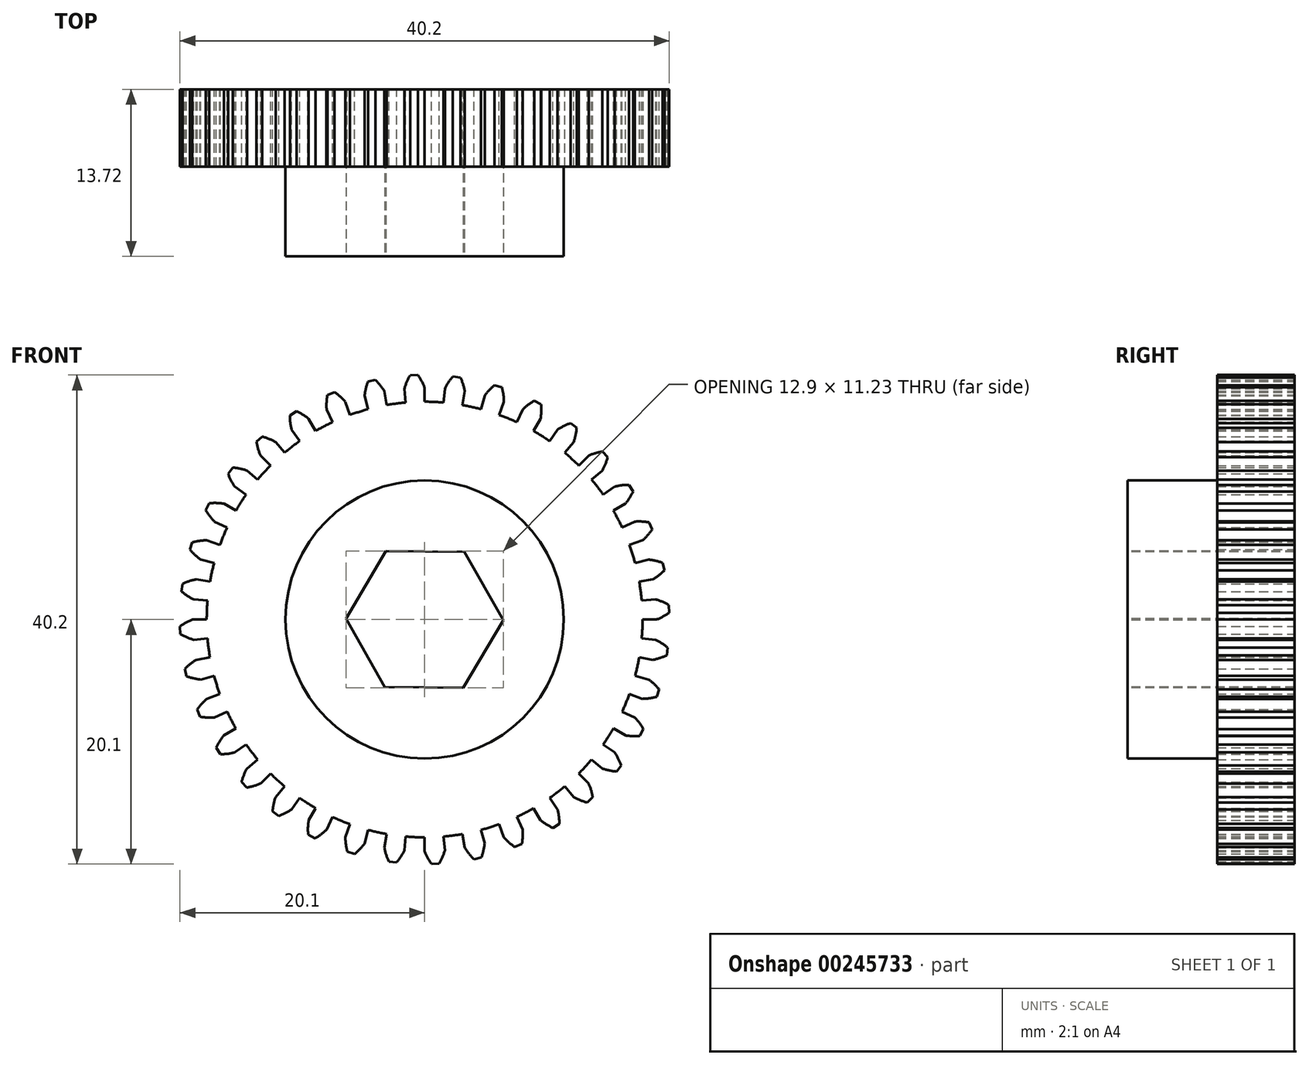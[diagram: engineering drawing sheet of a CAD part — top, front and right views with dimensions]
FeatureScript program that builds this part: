
annotation { "Feature Type Name" : "Feature", "Feature Type Description" : "" }
export const myFeature = defineFeature(function(context is Context, id is Id, definition is map)
    precondition{}
    {
        {
            var Q0;
            Q0=qCreatedBy(makeId("Front.planeOp"),FACE);
            var sketch = newSketch(context, id + "F0", { "sketchPlane" : qUnion([Q0])});
            skArc(sketch, "E0", {"start": v(-4.45, 17.34) * mm, "mid": v(-5.38, 17.07) * mm, "end": v(-6.3, 16.75) * mm});
            skLineSegment(sketch, "E1.trimOffspring", {"start": v(0, 23.81) * mm, "end": v(0, 30.83) * mm});
            skArc(sketch, "E2.trimOffspring", {"start": v(0, 19.05) * mm, "mid": v(-0.25, 19.6) * mm, "end": v(-0.56, 20.1) * mm});
            skArc(sketch, "E3.MirrorCS", {"start": v(-1.66, 18.98) * mm, "mid": v(-1.46, 19.54) * mm, "end": v(-1.2, 20.07) * mm});
            skLineSegment(sketch, "E4.trimOffspring", {"start": v(-1.56, 17.83) * mm, "end": v(-1.66, 18.98) * mm});
            skLineSegment(sketch, "E5.trimOffspring", {"start": v(0, 17.9) * mm, "end": v(0, 19.05) * mm});
            skArc(sketch, "E6.trimOffspring", {"start": v(0, 17.9) * mm, "mid": v(-0.1, 17.9) * mm, "end": v(-0.2, 17.9) * mm});
            skArc(sketch, "E7", {"start": v(-1.56, 17.84) * mm, "mid": v(-2.34, 17.75) * mm, "end": v(-3.1, 17.63) * mm});
            skLineSegment(sketch, "E8", {"start": v(-1.2, 20.07) * mm, "end": v(-0.56, 20.1) * mm});
            skLineSegment(sketch, "E9.1.0", {"start": v(-4.63, 17.3) * mm, "end": v(-4.93, 18.4) * mm});
            skArc(sketch, "E9.1.1", {"start": v(-4.93, 18.4) * mm, "mid": v(-4.83, 18.99) * mm, "end": v(-4.66, 19.56) * mm});
            skLineSegment(sketch, "E9.1.2", {"start": v(-4.66, 19.56) * mm, "end": v(-4.04, 19.7) * mm});
            skArc(sketch, "E9.1.3", {"start": v(-3.3, 18.76) * mm, "mid": v(-3.65, 19.25) * mm, "end": v(-4.04, 19.7) * mm});
            skLineSegment(sketch, "E9.1.4", {"start": v(-3.1, 17.63) * mm, "end": v(-3.3, 18.76) * mm});
            skLineSegment(sketch, "E9.2.0", {"start": v(-7.57, 16.22) * mm, "end": v(-8.05, 17.27) * mm});
            skArc(sketch, "E9.2.1", {"start": v(-8.05, 17.27) * mm, "mid": v(-8.05, 17.86) * mm, "end": v(-7.98, 18.45) * mm});
            skLineSegment(sketch, "E9.2.2", {"start": v(-7.98, 18.45) * mm, "end": v(-7.4, 18.7) * mm});
            skArc(sketch, "E9.2.3", {"start": v(-6.52, 17.9) * mm, "mid": v(-6.93, 18.32) * mm, "end": v(-7.4, 18.7) * mm});
            skLineSegment(sketch, "E9.2.4", {"start": v(-6.12, 16.82) * mm, "end": v(-6.52, 17.9) * mm});
            skLineSegment(sketch, "E9.3.0", {"start": v(-10.27, 14.66) * mm, "end": v(-10.93, 15.6) * mm});
            skArc(sketch, "E9.3.1", {"start": v(-10.93, 15.6) * mm, "mid": v(-11.03, 16.19) * mm, "end": v(-11.07, 16.78) * mm});
            skLineSegment(sketch, "E9.3.2", {"start": v(-11.07, 16.78) * mm, "end": v(-10.53, 17.12) * mm});
            skArc(sketch, "E9.3.3", {"start": v(-9.52, 16.5) * mm, "mid": v(-10, 16.84) * mm, "end": v(-10.53, 17.12) * mm});
            skLineSegment(sketch, "E9.3.4", {"start": v(-8.95, 15.5) * mm, "end": v(-9.53, 16.5) * mm});
            skLineSegment(sketch, "E9.4.0", {"start": v(-12.66, 12.66) * mm, "end": v(-13.47, 13.47) * mm});
            skArc(sketch, "E9.4.1", {"start": v(-13.47, 13.47) * mm, "mid": v(-13.68, 14.03) * mm, "end": v(-13.81, 14.6) * mm});
            skLineSegment(sketch, "E9.4.2", {"start": v(-13.81, 14.6) * mm, "end": v(-13.35, 15.03) * mm});
            skArc(sketch, "E9.4.3", {"start": v(-12.25, 14.6) * mm, "mid": v(-12.78, 14.85) * mm, "end": v(-13.35, 15.03) * mm});
            skLineSegment(sketch, "E9.4.4", {"start": v(-11.5, 13.71) * mm, "end": v(-12.25, 14.6) * mm});
            skLineSegment(sketch, "E9.5.0", {"start": v(-14.66, 10.27) * mm, "end": v(-15.6, 10.93) * mm});
            skArc(sketch, "E9.5.1", {"start": v(-15.6, 10.93) * mm, "mid": v(-15.9, 11.44) * mm, "end": v(-16.14, 11.99) * mm});
            skLineSegment(sketch, "E9.5.2", {"start": v(-16.14, 11.99) * mm, "end": v(-15.76, 12.49) * mm});
            skArc(sketch, "E9.5.3", {"start": v(-14.6, 12.25) * mm, "mid": v(-15.17, 12.4) * mm, "end": v(-15.76, 12.49) * mm});
            skLineSegment(sketch, "E9.5.4", {"start": v(-13.71, 11.5) * mm, "end": v(-14.6, 12.25) * mm});
            skLineSegment(sketch, "E9.6.0", {"start": v(-16.22, 7.57) * mm, "end": v(-17.27, 8.05) * mm});
            skArc(sketch, "E9.6.1", {"start": v(-17.27, 8.05) * mm, "mid": v(-17.65, 8.5) * mm, "end": v(-17.98, 9) * mm});
            skLineSegment(sketch, "E9.6.2", {"start": v(-17.98, 9) * mm, "end": v(-17.68, 9.56) * mm});
            skArc(sketch, "E9.6.3", {"start": v(-16.5, 9.53) * mm, "mid": v(-17.09, 9.58) * mm, "end": v(-17.68, 9.56) * mm});
            skLineSegment(sketch, "E9.6.4", {"start": v(-15.5, 8.95) * mm, "end": v(-16.5, 9.53) * mm});
            skLineSegment(sketch, "E9.7.0", {"start": v(-17.3, 4.63) * mm, "end": v(-18.4, 4.93) * mm});
            skArc(sketch, "E9.7.1", {"start": v(-18.4, 4.93) * mm, "mid": v(-18.86, 5.3) * mm, "end": v(-19.27, 5.74) * mm});
            skLineSegment(sketch, "E9.7.2", {"start": v(-19.27, 5.74) * mm, "end": v(-19.08, 6.35) * mm});
            skArc(sketch, "E9.7.3", {"start": v(-17.9, 6.52) * mm, "mid": v(-18.5, 6.47) * mm, "end": v(-19.08, 6.35) * mm});
            skLineSegment(sketch, "E9.7.4", {"start": v(-16.82, 6.12) * mm, "end": v(-17.9, 6.52) * mm});
            skLineSegment(sketch, "E9.8.0", {"start": v(-17.83, 1.56) * mm, "end": v(-18.98, 1.66) * mm});
            skArc(sketch, "E9.8.1", {"start": v(-18.98, 1.66) * mm, "mid": v(-19.5, 1.95) * mm, "end": v(-19.97, 2.31) * mm});
            skLineSegment(sketch, "E9.8.2", {"start": v(-19.97, 2.31) * mm, "end": v(-19.89, 2.94) * mm});
            skArc(sketch, "E9.8.3", {"start": v(-18.76, 3.3) * mm, "mid": v(-19.34, 3.16) * mm, "end": v(-19.89, 2.94) * mm});
            skLineSegment(sketch, "E9.8.4", {"start": v(-17.63, 3.1) * mm, "end": v(-18.76, 3.3) * mm});
            skLineSegment(sketch, "E9.9.0", {"start": v(-17.83, -1.56) * mm, "end": v(-18.98, -1.66) * mm});
            skArc(sketch, "E9.9.1", {"start": v(-18.98, -1.66) * mm, "mid": v(-19.54, -1.46) * mm, "end": v(-20.07, -1.2) * mm});
            skLineSegment(sketch, "E9.9.2", {"start": v(-20.07, -1.2) * mm, "end": v(-20.1, -0.56) * mm});
            skArc(sketch, "E9.9.3", {"start": v(-19.05, 0) * mm, "mid": v(-19.6, -0.25) * mm, "end": v(-20.1, -0.56) * mm});
            skLineSegment(sketch, "E9.9.4", {"start": v(-17.9, 0) * mm, "end": v(-19.05, 0) * mm});
            skLineSegment(sketch, "E9.10.0", {"start": v(-17.3, -4.63) * mm, "end": v(-18.4, -4.93) * mm});
            skArc(sketch, "E9.10.1", {"start": v(-18.4, -4.93) * mm, "mid": v(-18.99, -4.83) * mm, "end": v(-19.56, -4.66) * mm});
            skLineSegment(sketch, "E9.10.2", {"start": v(-19.56, -4.66) * mm, "end": v(-19.7, -4.04) * mm});
            skArc(sketch, "E9.10.3", {"start": v(-18.76, -3.3) * mm, "mid": v(-19.25, -3.65) * mm, "end": v(-19.7, -4.04) * mm});
            skLineSegment(sketch, "E9.10.4", {"start": v(-17.63, -3.1) * mm, "end": v(-18.76, -3.3) * mm});
            skLineSegment(sketch, "E9.11.0", {"start": v(-16.22, -7.57) * mm, "end": v(-17.27, -8.05) * mm});
            skArc(sketch, "E9.11.1", {"start": v(-17.27, -8.05) * mm, "mid": v(-17.86, -8.05) * mm, "end": v(-18.45, -7.98) * mm});
            skLineSegment(sketch, "E9.11.2", {"start": v(-18.45, -7.98) * mm, "end": v(-18.7, -7.4) * mm});
            skArc(sketch, "E9.11.3", {"start": v(-17.9, -6.52) * mm, "mid": v(-18.32, -6.93) * mm, "end": v(-18.7, -7.4) * mm});
            skLineSegment(sketch, "E9.11.4", {"start": v(-16.82, -6.12) * mm, "end": v(-17.9, -6.52) * mm});
            skLineSegment(sketch, "E9.12.0", {"start": v(-14.66, -10.27) * mm, "end": v(-15.6, -10.93) * mm});
            skArc(sketch, "E9.12.1", {"start": v(-15.6, -10.93) * mm, "mid": v(-16.19, -11.03) * mm, "end": v(-16.78, -11.07) * mm});
            skLineSegment(sketch, "E9.12.2", {"start": v(-16.78, -11.07) * mm, "end": v(-17.12, -10.53) * mm});
            skArc(sketch, "E9.12.3", {"start": v(-16.5, -9.52) * mm, "mid": v(-16.84, -10) * mm, "end": v(-17.12, -10.53) * mm});
            skLineSegment(sketch, "E9.12.4", {"start": v(-15.5, -8.95) * mm, "end": v(-16.5, -9.52) * mm});
            skLineSegment(sketch, "E9.13.0", {"start": v(-12.66, -12.66) * mm, "end": v(-13.47, -13.47) * mm});
            skArc(sketch, "E9.13.1", {"start": v(-13.47, -13.47) * mm, "mid": v(-14.03, -13.68) * mm, "end": v(-14.6, -13.81) * mm});
            skLineSegment(sketch, "E9.13.2", {"start": v(-14.6, -13.81) * mm, "end": v(-15.03, -13.35) * mm});
            skArc(sketch, "E9.13.3", {"start": v(-14.6, -12.25) * mm, "mid": v(-14.85, -12.78) * mm, "end": v(-15.03, -13.35) * mm});
            skLineSegment(sketch, "E9.13.4", {"start": v(-13.71, -11.5) * mm, "end": v(-14.6, -12.25) * mm});
            skLineSegment(sketch, "E9.14.0", {"start": v(-10.27, -14.66) * mm, "end": v(-10.93, -15.6) * mm});
            skArc(sketch, "E9.14.1", {"start": v(-10.93, -15.6) * mm, "mid": v(-11.44, -15.9) * mm, "end": v(-11.99, -16.14) * mm});
            skLineSegment(sketch, "E9.14.2", {"start": v(-11.99, -16.14) * mm, "end": v(-12.49, -15.76) * mm});
            skArc(sketch, "E9.14.3", {"start": v(-12.25, -14.6) * mm, "mid": v(-12.4, -15.17) * mm, "end": v(-12.49, -15.76) * mm});
            skLineSegment(sketch, "E9.14.4", {"start": v(-11.5, -13.71) * mm, "end": v(-12.25, -14.6) * mm});
            skLineSegment(sketch, "E9.15.0", {"start": v(-7.57, -16.22) * mm, "end": v(-8.05, -17.27) * mm});
            skArc(sketch, "E9.15.1", {"start": v(-8.05, -17.27) * mm, "mid": v(-8.5, -17.65) * mm, "end": v(-9, -17.98) * mm});
            skLineSegment(sketch, "E9.15.2", {"start": v(-9, -17.98) * mm, "end": v(-9.56, -17.68) * mm});
            skArc(sketch, "E9.15.3", {"start": v(-9.53, -16.5) * mm, "mid": v(-9.58, -17.09) * mm, "end": v(-9.56, -17.68) * mm});
            skLineSegment(sketch, "E9.15.4", {"start": v(-8.95, -15.5) * mm, "end": v(-9.53, -16.5) * mm});
            skLineSegment(sketch, "E9.16.0", {"start": v(-4.63, -17.3) * mm, "end": v(-4.93, -18.4) * mm});
            skArc(sketch, "E9.16.1", {"start": v(-4.93, -18.4) * mm, "mid": v(-5.3, -18.86) * mm, "end": v(-5.74, -19.27) * mm});
            skLineSegment(sketch, "E9.16.2", {"start": v(-5.74, -19.27) * mm, "end": v(-6.35, -19.08) * mm});
            skArc(sketch, "E9.16.3", {"start": v(-6.52, -17.9) * mm, "mid": v(-6.47, -18.5) * mm, "end": v(-6.35, -19.08) * mm});
            skLineSegment(sketch, "E9.16.4", {"start": v(-6.12, -16.82) * mm, "end": v(-6.52, -17.9) * mm});
            skLineSegment(sketch, "E9.17.0", {"start": v(-1.56, -17.83) * mm, "end": v(-1.66, -18.98) * mm});
            skArc(sketch, "E9.17.1", {"start": v(-1.66, -18.98) * mm, "mid": v(-1.95, -19.5) * mm, "end": v(-2.31, -19.97) * mm});
            skLineSegment(sketch, "E9.17.2", {"start": v(-2.31, -19.97) * mm, "end": v(-2.94, -19.89) * mm});
            skArc(sketch, "E9.17.3", {"start": v(-3.3, -18.76) * mm, "mid": v(-3.16, -19.34) * mm, "end": v(-2.94, -19.89) * mm});
            skLineSegment(sketch, "E9.17.4", {"start": v(-3.1, -17.63) * mm, "end": v(-3.3, -18.76) * mm});
            skLineSegment(sketch, "E9.18.0", {"start": v(1.56, -17.83) * mm, "end": v(1.66, -18.98) * mm});
            skArc(sketch, "E9.18.1", {"start": v(1.66, -18.98) * mm, "mid": v(1.46, -19.54) * mm, "end": v(1.2, -20.07) * mm});
            skLineSegment(sketch, "E9.18.2", {"start": v(1.2, -20.07) * mm, "end": v(0.56, -20.1) * mm});
            skArc(sketch, "E9.18.3", {"start": v(0, -19.05) * mm, "mid": v(0.25, -19.6) * mm, "end": v(0.56, -20.1) * mm});
            skLineSegment(sketch, "E9.18.4", {"start": v(0, -17.9) * mm, "end": v(0, -19.05) * mm});
            skLineSegment(sketch, "E9.19.0", {"start": v(4.63, -17.3) * mm, "end": v(4.93, -18.4) * mm});
            skArc(sketch, "E9.19.1", {"start": v(4.93, -18.4) * mm, "mid": v(4.83, -18.99) * mm, "end": v(4.66, -19.56) * mm});
            skLineSegment(sketch, "E9.19.2", {"start": v(4.66, -19.56) * mm, "end": v(4.04, -19.7) * mm});
            skArc(sketch, "E9.19.3", {"start": v(3.3, -18.76) * mm, "mid": v(3.65, -19.25) * mm, "end": v(4.04, -19.7) * mm});
            skLineSegment(sketch, "E9.19.4", {"start": v(3.1, -17.63) * mm, "end": v(3.3, -18.76) * mm});
            skLineSegment(sketch, "E9.20.0", {"start": v(7.57, -16.22) * mm, "end": v(8.05, -17.27) * mm});
            skArc(sketch, "E9.20.1", {"start": v(8.05, -17.27) * mm, "mid": v(8.05, -17.86) * mm, "end": v(7.98, -18.45) * mm});
            skLineSegment(sketch, "E9.20.2", {"start": v(7.98, -18.45) * mm, "end": v(7.4, -18.7) * mm});
            skArc(sketch, "E9.20.3", {"start": v(6.52, -17.9) * mm, "mid": v(6.93, -18.32) * mm, "end": v(7.4, -18.7) * mm});
            skLineSegment(sketch, "E9.20.4", {"start": v(6.12, -16.82) * mm, "end": v(6.52, -17.9) * mm});
            skLineSegment(sketch, "E9.21.0", {"start": v(10.27, -14.66) * mm, "end": v(10.93, -15.6) * mm});
            skArc(sketch, "E9.21.1", {"start": v(10.93, -15.6) * mm, "mid": v(11.03, -16.19) * mm, "end": v(11.07, -16.78) * mm});
            skLineSegment(sketch, "E9.21.2", {"start": v(11.07, -16.78) * mm, "end": v(10.53, -17.12) * mm});
            skArc(sketch, "E9.21.3", {"start": v(9.52, -16.5) * mm, "mid": v(10, -16.84) * mm, "end": v(10.53, -17.12) * mm});
            skLineSegment(sketch, "E9.21.4", {"start": v(8.95, -15.5) * mm, "end": v(9.53, -16.5) * mm});
            skLineSegment(sketch, "E9.22.0", {"start": v(12.66, -12.66) * mm, "end": v(13.47, -13.47) * mm});
            skArc(sketch, "E9.22.1", {"start": v(13.47, -13.47) * mm, "mid": v(13.68, -14.03) * mm, "end": v(13.81, -14.6) * mm});
            skLineSegment(sketch, "E9.22.2", {"start": v(13.81, -14.6) * mm, "end": v(13.35, -15.03) * mm});
            skArc(sketch, "E9.22.3", {"start": v(12.25, -14.6) * mm, "mid": v(12.78, -14.85) * mm, "end": v(13.35, -15.03) * mm});
            skLineSegment(sketch, "E9.22.4", {"start": v(11.5, -13.71) * mm, "end": v(12.25, -14.6) * mm});
            skLineSegment(sketch, "E9.23.0", {"start": v(14.66, -10.27) * mm, "end": v(15.6, -10.93) * mm});
            skArc(sketch, "E9.23.1", {"start": v(15.6, -10.93) * mm, "mid": v(15.9, -11.44) * mm, "end": v(16.14, -11.99) * mm});
            skLineSegment(sketch, "E9.23.2", {"start": v(16.14, -11.99) * mm, "end": v(15.76, -12.49) * mm});
            skArc(sketch, "E9.23.3", {"start": v(14.6, -12.25) * mm, "mid": v(15.17, -12.4) * mm, "end": v(15.76, -12.49) * mm});
            skLineSegment(sketch, "E9.23.4", {"start": v(13.71, -11.5) * mm, "end": v(14.6, -12.25) * mm});
            skLineSegment(sketch, "E9.24.0", {"start": v(16.22, -7.57) * mm, "end": v(17.27, -8.05) * mm});
            skArc(sketch, "E9.24.1", {"start": v(17.27, -8.05) * mm, "mid": v(17.65, -8.5) * mm, "end": v(17.98, -9) * mm});
            skLineSegment(sketch, "E9.24.2", {"start": v(17.98, -9) * mm, "end": v(17.68, -9.56) * mm});
            skArc(sketch, "E9.24.3", {"start": v(16.5, -9.53) * mm, "mid": v(17.09, -9.58) * mm, "end": v(17.68, -9.56) * mm});
            skLineSegment(sketch, "E9.24.4", {"start": v(15.5, -8.95) * mm, "end": v(16.5, -9.53) * mm});
            skLineSegment(sketch, "E9.25.0", {"start": v(17.3, -4.63) * mm, "end": v(18.4, -4.93) * mm});
            skArc(sketch, "E9.25.1", {"start": v(18.4, -4.93) * mm, "mid": v(18.86, -5.3) * mm, "end": v(19.27, -5.74) * mm});
            skLineSegment(sketch, "E9.25.2", {"start": v(19.27, -5.74) * mm, "end": v(19.08, -6.35) * mm});
            skArc(sketch, "E9.25.3", {"start": v(17.9, -6.52) * mm, "mid": v(18.5, -6.47) * mm, "end": v(19.08, -6.35) * mm});
            skLineSegment(sketch, "E9.25.4", {"start": v(16.82, -6.12) * mm, "end": v(17.9, -6.52) * mm});
            skLineSegment(sketch, "E9.26.0", {"start": v(17.83, -1.56) * mm, "end": v(18.98, -1.66) * mm});
            skArc(sketch, "E9.26.1", {"start": v(18.98, -1.66) * mm, "mid": v(19.5, -1.95) * mm, "end": v(19.97, -2.31) * mm});
            skLineSegment(sketch, "E9.26.2", {"start": v(19.97, -2.31) * mm, "end": v(19.89, -2.94) * mm});
            skArc(sketch, "E9.26.3", {"start": v(18.76, -3.3) * mm, "mid": v(19.34, -3.16) * mm, "end": v(19.89, -2.94) * mm});
            skLineSegment(sketch, "E9.26.4", {"start": v(17.63, -3.1) * mm, "end": v(18.76, -3.3) * mm});
            skLineSegment(sketch, "E9.27.0", {"start": v(17.83, 1.56) * mm, "end": v(18.98, 1.66) * mm});
            skArc(sketch, "E9.27.1", {"start": v(18.98, 1.66) * mm, "mid": v(19.54, 1.46) * mm, "end": v(20.07, 1.2) * mm});
            skLineSegment(sketch, "E9.27.2", {"start": v(20.07, 1.2) * mm, "end": v(20.1, 0.56) * mm});
            skArc(sketch, "E9.27.3", {"start": v(19.05, 0) * mm, "mid": v(19.6, 0.25) * mm, "end": v(20.1, 0.56) * mm});
            skLineSegment(sketch, "E9.27.4", {"start": v(17.9, 0) * mm, "end": v(19.05, 0) * mm});
            skLineSegment(sketch, "E9.28.0", {"start": v(17.3, 4.63) * mm, "end": v(18.4, 4.93) * mm});
            skArc(sketch, "E9.28.1", {"start": v(18.4, 4.93) * mm, "mid": v(18.99, 4.83) * mm, "end": v(19.56, 4.66) * mm});
            skLineSegment(sketch, "E9.28.2", {"start": v(19.56, 4.66) * mm, "end": v(19.7, 4.04) * mm});
            skArc(sketch, "E9.28.3", {"start": v(18.76, 3.3) * mm, "mid": v(19.25, 3.65) * mm, "end": v(19.7, 4.04) * mm});
            skLineSegment(sketch, "E9.28.4", {"start": v(17.63, 3.1) * mm, "end": v(18.76, 3.3) * mm});
            skLineSegment(sketch, "E9.29.0", {"start": v(16.22, 7.57) * mm, "end": v(17.27, 8.05) * mm});
            skArc(sketch, "E9.29.1", {"start": v(17.27, 8.05) * mm, "mid": v(17.86, 8.05) * mm, "end": v(18.45, 7.98) * mm});
            skLineSegment(sketch, "E9.29.2", {"start": v(18.45, 7.98) * mm, "end": v(18.7, 7.4) * mm});
            skArc(sketch, "E9.29.3", {"start": v(17.9, 6.52) * mm, "mid": v(18.32, 6.93) * mm, "end": v(18.7, 7.4) * mm});
            skLineSegment(sketch, "E9.29.4", {"start": v(16.82, 6.12) * mm, "end": v(17.9, 6.52) * mm});
            skLineSegment(sketch, "E9.30.0", {"start": v(14.66, 10.27) * mm, "end": v(15.6, 10.93) * mm});
            skArc(sketch, "E9.30.1", {"start": v(15.6, 10.93) * mm, "mid": v(16.19, 11.03) * mm, "end": v(16.78, 11.07) * mm});
            skLineSegment(sketch, "E9.30.2", {"start": v(16.78, 11.07) * mm, "end": v(17.12, 10.53) * mm});
            skArc(sketch, "E9.30.3", {"start": v(16.5, 9.52) * mm, "mid": v(16.84, 10) * mm, "end": v(17.12, 10.53) * mm});
            skLineSegment(sketch, "E9.30.4", {"start": v(15.5, 8.95) * mm, "end": v(16.5, 9.52) * mm});
            skLineSegment(sketch, "E9.31.0", {"start": v(12.66, 12.66) * mm, "end": v(13.47, 13.47) * mm});
            skArc(sketch, "E9.31.1", {"start": v(13.47, 13.47) * mm, "mid": v(14.03, 13.68) * mm, "end": v(14.6, 13.81) * mm});
            skLineSegment(sketch, "E9.31.2", {"start": v(14.6, 13.81) * mm, "end": v(15.03, 13.35) * mm});
            skArc(sketch, "E9.31.3", {"start": v(14.6, 12.25) * mm, "mid": v(14.85, 12.78) * mm, "end": v(15.03, 13.35) * mm});
            skLineSegment(sketch, "E9.31.4", {"start": v(13.71, 11.5) * mm, "end": v(14.6, 12.25) * mm});
            skLineSegment(sketch, "E9.32.0", {"start": v(10.27, 14.66) * mm, "end": v(10.93, 15.6) * mm});
            skArc(sketch, "E9.32.1", {"start": v(10.93, 15.6) * mm, "mid": v(11.44, 15.9) * mm, "end": v(11.99, 16.14) * mm});
            skLineSegment(sketch, "E9.32.2", {"start": v(11.99, 16.14) * mm, "end": v(12.49, 15.76) * mm});
            skArc(sketch, "E9.32.3", {"start": v(12.25, 14.6) * mm, "mid": v(12.4, 15.17) * mm, "end": v(12.49, 15.76) * mm});
            skLineSegment(sketch, "E9.32.4", {"start": v(11.5, 13.71) * mm, "end": v(12.25, 14.6) * mm});
            skLineSegment(sketch, "E9.33.0", {"start": v(7.57, 16.22) * mm, "end": v(8.05, 17.27) * mm});
            skArc(sketch, "E9.33.1", {"start": v(8.05, 17.27) * mm, "mid": v(8.5, 17.65) * mm, "end": v(9, 17.98) * mm});
            skLineSegment(sketch, "E9.33.2", {"start": v(9, 17.98) * mm, "end": v(9.56, 17.68) * mm});
            skArc(sketch, "E9.33.3", {"start": v(9.53, 16.5) * mm, "mid": v(9.58, 17.09) * mm, "end": v(9.56, 17.68) * mm});
            skLineSegment(sketch, "E9.33.4", {"start": v(8.95, 15.5) * mm, "end": v(9.52, 16.5) * mm});
            skLineSegment(sketch, "E9.34.0", {"start": v(4.63, 17.3) * mm, "end": v(4.93, 18.4) * mm});
            skArc(sketch, "E9.34.1", {"start": v(4.93, 18.4) * mm, "mid": v(5.3, 18.86) * mm, "end": v(5.74, 19.27) * mm});
            skLineSegment(sketch, "E9.34.2", {"start": v(5.74, 19.27) * mm, "end": v(6.35, 19.08) * mm});
            skArc(sketch, "E9.34.3", {"start": v(6.52, 17.9) * mm, "mid": v(6.47, 18.5) * mm, "end": v(6.35, 19.08) * mm});
            skLineSegment(sketch, "E9.34.4", {"start": v(6.12, 16.82) * mm, "end": v(6.52, 17.9) * mm});
            skLineSegment(sketch, "E9.35.0", {"start": v(1.56, 17.83) * mm, "end": v(1.66, 18.98) * mm});
            skArc(sketch, "E9.35.1", {"start": v(1.66, 18.98) * mm, "mid": v(1.95, 19.5) * mm, "end": v(2.31, 19.97) * mm});
            skLineSegment(sketch, "E9.35.2", {"start": v(2.31, 19.97) * mm, "end": v(2.94, 19.89) * mm});
            skArc(sketch, "E9.35.3", {"start": v(3.3, 18.76) * mm, "mid": v(3.16, 19.34) * mm, "end": v(2.94, 19.89) * mm});
            skLineSegment(sketch, "E9.35.4", {"start": v(3.1, 17.63) * mm, "end": v(3.3, 18.76) * mm});
            skArc(sketch, "E10.trimOffspring", {"start": v(-1.37, 17.85) * mm, "mid": v(-1.46, 17.84) * mm, "end": v(-1.56, 17.83) * mm});
            skArc(sketch, "E11.trimOffspring", {"start": v(1.56, 17.84) * mm, "mid": v(0.78, 17.89) * mm, "end": v(0, 17.9) * mm});
            skArc(sketch, "E12.trimOffspring", {"start": v(4.63, 17.3) * mm, "mid": v(3.88, 17.48) * mm, "end": v(3.1, 17.63) * mm});
            skArc(sketch, "E13.trimOffspring", {"start": v(4.82, 17.24) * mm, "mid": v(3.87, 17.48) * mm, "end": v(2.92, 17.66) * mm});
            skArc(sketch, "E14.trimOffspring", {"start": v(7.57, 16.23) * mm, "mid": v(6.85, 16.54) * mm, "end": v(6.12, 16.82) * mm});
            skArc(sketch, "E15.trimOffspring", {"start": v(7.74, 16.14) * mm, "mid": v(6.85, 16.54) * mm, "end": v(5.94, 16.89) * mm});
            skArc(sketch, "E16.trimOffspring", {"start": v(10.27, 14.67) * mm, "mid": v(9.62, 15.1) * mm, "end": v(8.95, 15.5) * mm});
            skArc(sketch, "E17.trimOffspring", {"start": v(10.43, 14.55) * mm, "mid": v(9.62, 15.1) * mm, "end": v(8.78, 15.6) * mm});
            skArc(sketch, "E18.trimOffspring", {"start": v(12.8, 12.52) * mm, "mid": v(12.1, 13.2) * mm, "end": v(11.36, 13.84) * mm});
            skArc(sketch, "E19.trimOffspring", {"start": v(14.67, 10.27) * mm, "mid": v(14.2, 10.9) * mm, "end": v(13.72, 11.5) * mm});
            skArc(sketch, "E20.trimOffspring", {"start": v(14.77, 10.1) * mm, "mid": v(14.2, 10.9) * mm, "end": v(13.59, 11.65) * mm});
            skArc(sketch, "E21.trimOffspring", {"start": v(16.23, 7.57) * mm, "mid": v(15.88, 8.27) * mm, "end": v(15.5, 8.95) * mm});
            skArc(sketch, "E22.trimOffspring", {"start": v(16.3, 7.39) * mm, "mid": v(15.88, 8.27) * mm, "end": v(15.4, 9.12) * mm});
            skArc(sketch, "E23.trimOffspring", {"start": v(17.34, 4.45) * mm, "mid": v(17.07, 5.38) * mm, "end": v(16.75, 6.3) * mm});
            skArc(sketch, "E24.trimOffspring", {"start": v(17.84, 1.56) * mm, "mid": v(17.75, 2.34) * mm, "end": v(17.63, 3.1) * mm});
            skArc(sketch, "E25.trimOffspring", {"start": v(17.85, 1.37) * mm, "mid": v(17.75, 2.34) * mm, "end": v(17.6, 3.3) * mm});
            skArc(sketch, "E26.trimOffspring", {"start": v(17.84, -1.56) * mm, "mid": v(17.89, -0.78) * mm, "end": v(17.9, 0) * mm});
            skArc(sketch, "E27.trimOffspring", {"start": v(17.82, -1.75) * mm, "mid": v(17.88, -0.78) * mm, "end": v(17.9, 0.2) * mm});
            skArc(sketch, "E28.trimOffspring", {"start": v(17.24, -4.82) * mm, "mid": v(17.48, -3.87) * mm, "end": v(17.66, -2.92) * mm});
            skArc(sketch, "E29.trimOffspring", {"start": v(16.23, -7.57) * mm, "mid": v(16.54, -6.85) * mm, "end": v(16.82, -6.12) * mm});
            skArc(sketch, "E30.trimOffspring", {"start": v(16.14, -7.74) * mm, "mid": v(16.54, -6.85) * mm, "end": v(16.89, -5.94) * mm});
            skArc(sketch, "E31.trimOffspring", {"start": v(14.55, -10.43) * mm, "mid": v(15.1, -9.62) * mm, "end": v(15.6, -8.78) * mm});
            skArc(sketch, "E32.trimOffspring", {"start": v(12.66, -12.66) * mm, "mid": v(13.2, -12.1) * mm, "end": v(13.72, -11.5) * mm});
            skArc(sketch, "E33.trimOffspring", {"start": v(12.52, -12.8) * mm, "mid": v(13.2, -12.1) * mm, "end": v(13.84, -11.36) * mm});
            skArc(sketch, "E34.trimOffspring", {"start": v(10.27, -14.67) * mm, "mid": v(10.9, -14.2) * mm, "end": v(11.5, -13.72) * mm});
            skArc(sketch, "E35.trimOffspring", {"start": v(10.1, -14.77) * mm, "mid": v(10.9, -14.2) * mm, "end": v(11.65, -13.59) * mm});
            skArc(sketch, "E36.trimOffspring", {"start": v(7.57, -16.23) * mm, "mid": v(8.27, -15.88) * mm, "end": v(8.95, -15.5) * mm});
            skArc(sketch, "E37.trimOffspring", {"start": v(7.39, -16.3) * mm, "mid": v(8.27, -15.88) * mm, "end": v(9.12, -15.4) * mm});
            skArc(sketch, "E38.trimOffspring", {"start": v(4.63, -17.3) * mm, "mid": v(5.38, -17.08) * mm, "end": v(6.12, -16.82) * mm});
            skArc(sketch, "E39.trimOffspring", {"start": v(4.45, -17.34) * mm, "mid": v(5.38, -17.07) * mm, "end": v(6.3, -16.75) * mm});
            skArc(sketch, "E40.trimOffspring", {"start": v(1.56, -17.84) * mm, "mid": v(2.34, -17.75) * mm, "end": v(3.1, -17.63) * mm});
            skArc(sketch, "E41.trimOffspring", {"start": v(1.37, -17.85) * mm, "mid": v(2.34, -17.75) * mm, "end": v(3.3, -17.6) * mm});
            skArc(sketch, "E42.trimOffspring", {"start": v(-1.56, -17.84) * mm, "mid": v(-0.78, -17.89) * mm, "end": v(0, -17.9) * mm});
            skArc(sketch, "E43.trimOffspring", {"start": v(-1.75, -17.82) * mm, "mid": v(-0.78, -17.88) * mm, "end": v(0.2, -17.9) * mm});
            skArc(sketch, "E44.trimOffspring", {"start": v(-4.63, -17.3) * mm, "mid": v(-3.88, -17.48) * mm, "end": v(-3.1, -17.63) * mm});
            skArc(sketch, "E45.trimOffspring", {"start": v(-4.82, -17.24) * mm, "mid": v(-3.87, -17.48) * mm, "end": v(-2.92, -17.66) * mm});
            skArc(sketch, "E46.trimOffspring", {"start": v(-7.57, -16.23) * mm, "mid": v(-6.85, -16.54) * mm, "end": v(-6.12, -16.82) * mm});
            skArc(sketch, "E47.trimOffspring", {"start": v(-7.74, -16.14) * mm, "mid": v(-6.94, -16.5) * mm, "end": v(-6.12, -16.82) * mm});
            skArc(sketch, "E48.trimOffspring", {"start": v(-10.43, -14.55) * mm, "mid": v(-9.62, -15.1) * mm, "end": v(-8.78, -15.6) * mm});
            skArc(sketch, "E49.trimOffspring", {"start": v(-12.66, -12.66) * mm, "mid": v(-12.1, -13.2) * mm, "end": v(-11.5, -13.72) * mm});
            skArc(sketch, "E50.trimOffspring", {"start": v(-12.8, -12.52) * mm, "mid": v(-12.1, -13.2) * mm, "end": v(-11.36, -13.84) * mm});
            skArc(sketch, "E51.trimOffspring", {"start": v(-14.67, -10.27) * mm, "mid": v(-14.2, -10.9) * mm, "end": v(-13.72, -11.5) * mm});
            skArc(sketch, "E52.trimOffspring", {"start": v(-14.77, -10.1) * mm, "mid": v(-14.2, -10.9) * mm, "end": v(-13.59, -11.65) * mm});
            skArc(sketch, "E53.trimOffspring", {"start": v(-16.23, -7.57) * mm, "mid": v(-15.88, -8.27) * mm, "end": v(-15.5, -8.95) * mm});
            skArc(sketch, "E54.trimOffspring", {"start": v(-16.3, -7.39) * mm, "mid": v(-15.88, -8.27) * mm, "end": v(-15.4, -9.12) * mm});
            skArc(sketch, "E55.trimOffspring", {"start": v(-17.3, -4.63) * mm, "mid": v(-17.08, -5.38) * mm, "end": v(-16.82, -6.12) * mm});
            skArc(sketch, "E56.trimOffspring", {"start": v(-17.34, -4.45) * mm, "mid": v(-17.07, -5.38) * mm, "end": v(-16.75, -6.3) * mm});
            skArc(sketch, "E57.trimOffspring", {"start": v(-17.84, -1.56) * mm, "mid": v(-17.75, -2.34) * mm, "end": v(-17.63, -3.1) * mm});
            skArc(sketch, "E58.trimOffspring", {"start": v(-17.85, -1.37) * mm, "mid": v(-17.75, -2.34) * mm, "end": v(-17.6, -3.3) * mm});
            skArc(sketch, "E59.trimOffspring", {"start": v(-17.84, 1.56) * mm, "mid": v(-17.89, 0.78) * mm, "end": v(-17.9, 0) * mm});
            skArc(sketch, "E60.trimOffspring", {"start": v(-17.82, 1.75) * mm, "mid": v(-17.88, 0.78) * mm, "end": v(-17.9, -0.2) * mm});
            skArc(sketch, "E61.trimOffspring", {"start": v(-17.3, 4.63) * mm, "mid": v(-17.48, 3.88) * mm, "end": v(-17.63, 3.1) * mm});
            skArc(sketch, "E62.trimOffspring", {"start": v(-17.24, 4.82) * mm, "mid": v(-17.48, 3.87) * mm, "end": v(-17.66, 2.92) * mm});
            skArc(sketch, "E63.trimOffspring", {"start": v(-16.23, 7.57) * mm, "mid": v(-16.54, 6.85) * mm, "end": v(-16.82, 6.12) * mm});
            skArc(sketch, "E64.trimOffspring", {"start": v(-16.14, 7.74) * mm, "mid": v(-16.54, 6.85) * mm, "end": v(-16.89, 5.94) * mm});
            skArc(sketch, "E65.trimOffspring", {"start": v(-14.55, 10.43) * mm, "mid": v(-15.1, 9.62) * mm, "end": v(-15.6, 8.78) * mm});
            skArc(sketch, "E66.trimOffspring", {"start": v(-12.66, 12.66) * mm, "mid": v(-13.2, 12.1) * mm, "end": v(-13.72, 11.5) * mm});
            skArc(sketch, "E67.trimOffspring", {"start": v(-12.52, 12.8) * mm, "mid": v(-13.2, 12.1) * mm, "end": v(-13.84, 11.36) * mm});
            skArc(sketch, "E68.trimOffspring", {"start": v(-10.27, 14.67) * mm, "mid": v(-10.9, 14.2) * mm, "end": v(-11.5, 13.72) * mm});
            skArc(sketch, "E69.trimOffspring", {"start": v(-10.1, 14.77) * mm, "mid": v(-10.9, 14.2) * mm, "end": v(-11.65, 13.59) * mm});
            skArc(sketch, "E70.trimOffspring", {"start": v(-7.57, 16.23) * mm, "mid": v(-8.27, 15.88) * mm, "end": v(-8.95, 15.5) * mm});
            skArc(sketch, "E71.trimOffspring", {"start": v(-7.39, 16.3) * mm, "mid": v(-8.27, 15.88) * mm, "end": v(-9.12, 15.4) * mm});
            skArc(sketch, "E72.trimOffspring", {"start": v(-4.63, 17.3) * mm, "mid": v(-5.38, 17.08) * mm, "end": v(-6.12, 16.82) * mm});
            skSolve(sketch);
        }
        {
            var Q0;
            {var subQ194=sQuery(id+"F0.wireOp",EDGE,"E2.trimOffspring");Q0=makeQuery(id+"F0.imprint","IMPRINT",FACE,{"disambiguationData":[TD([[makeQuery(id+"F0.imprint","IMPRINT",EDGE,{"derivedFrom":subQ194}),1.0]])]});}
            extrude(context, id + "F1", {"entities" : qUnion([Q0]), "depth" : 6.35 * mm});
        }
        {
            var Q0;
            Q0=makeQuery(id+"F1.opExtrude","CAP_FACE",FACE,{"disambiguationData":[OSD([sQuery(id+"F0.wireOp",EDGE,"E0"),sQuery(id+"F0.wireOp",EDGE,"E2.trimOffspring"),sQuery(id+"F0.wireOp",EDGE,"E3.MirrorCS"),sQuery(id+"F0.wireOp",EDGE,"E4.trimOffspring"),sQuery(id+"F0.wireOp",EDGE,"E5.trimOffspring"),sQuery(id+"F0.wireOp",EDGE,"E7"),sQuery(id+"F0.wireOp",EDGE,"E8"),sQuery(id+"F0.wireOp",EDGE,"E9.1.0"),sQuery(id+"F0.wireOp",EDGE,"E9.1.1"),sQuery(id+"F0.wireOp",EDGE,"E9.1.2"),sQuery(id+"F0.wireOp",EDGE,"E9.1.3"),sQuery(id+"F0.wireOp",EDGE,"E9.1.4"),sQuery(id+"F0.wireOp",EDGE,"E9.2.0"),sQuery(id+"F0.wireOp",EDGE,"E9.2.1"),sQuery(id+"F0.wireOp",EDGE,"E9.2.2"),sQuery(id+"F0.wireOp",EDGE,"E9.2.3"),sQuery(id+"F0.wireOp",EDGE,"E9.2.4"),sQuery(id+"F0.wireOp",EDGE,"E9.3.0"),sQuery(id+"F0.wireOp",EDGE,"E9.3.1"),sQuery(id+"F0.wireOp",EDGE,"E9.3.2"),sQuery(id+"F0.wireOp",EDGE,"E9.3.3"),sQuery(id+"F0.wireOp",EDGE,"E9.3.4"),sQuery(id+"F0.wireOp",EDGE,"E9.4.0"),sQuery(id+"F0.wireOp",EDGE,"E9.4.1"),sQuery(id+"F0.wireOp",EDGE,"E9.4.2"),sQuery(id+"F0.wireOp",EDGE,"E9.4.3"),sQuery(id+"F0.wireOp",EDGE,"E9.4.4"),sQuery(id+"F0.wireOp",EDGE,"E9.5.0"),sQuery(id+"F0.wireOp",EDGE,"E9.5.1"),sQuery(id+"F0.wireOp",EDGE,"E9.5.2"),sQuery(id+"F0.wireOp",EDGE,"E9.5.3"),sQuery(id+"F0.wireOp",EDGE,"E9.5.4"),sQuery(id+"F0.wireOp",EDGE,"E9.6.0"),sQuery(id+"F0.wireOp",EDGE,"E9.6.1"),sQuery(id+"F0.wireOp",EDGE,"E9.6.2"),sQuery(id+"F0.wireOp",EDGE,"E9.6.3"),sQuery(id+"F0.wireOp",EDGE,"E9.6.4"),sQuery(id+"F0.wireOp",EDGE,"E9.7.0"),sQuery(id+"F0.wireOp",EDGE,"E9.7.1"),sQuery(id+"F0.wireOp",EDGE,"E9.7.2"),sQuery(id+"F0.wireOp",EDGE,"E9.7.3"),sQuery(id+"F0.wireOp",EDGE,"E9.7.4"),sQuery(id+"F0.wireOp",EDGE,"E9.8.0"),sQuery(id+"F0.wireOp",EDGE,"E9.8.1"),sQuery(id+"F0.wireOp",EDGE,"E9.8.2"),sQuery(id+"F0.wireOp",EDGE,"E9.8.3"),sQuery(id+"F0.wireOp",EDGE,"E9.8.4"),sQuery(id+"F0.wireOp",EDGE,"E9.9.0"),sQuery(id+"F0.wireOp",EDGE,"E9.9.1"),sQuery(id+"F0.wireOp",EDGE,"E9.9.2"),sQuery(id+"F0.wireOp",EDGE,"E9.9.3"),sQuery(id+"F0.wireOp",EDGE,"E9.9.4"),sQuery(id+"F0.wireOp",EDGE,"E9.10.0"),sQuery(id+"F0.wireOp",EDGE,"E9.10.1"),sQuery(id+"F0.wireOp",EDGE,"E9.10.2"),sQuery(id+"F0.wireOp",EDGE,"E9.10.3"),sQuery(id+"F0.wireOp",EDGE,"E9.10.4"),sQuery(id+"F0.wireOp",EDGE,"E9.11.0"),sQuery(id+"F0.wireOp",EDGE,"E9.11.1"),sQuery(id+"F0.wireOp",EDGE,"E9.11.2"),sQuery(id+"F0.wireOp",EDGE,"E9.11.3"),sQuery(id+"F0.wireOp",EDGE,"E9.11.4"),sQuery(id+"F0.wireOp",EDGE,"E9.12.0"),sQuery(id+"F0.wireOp",EDGE,"E9.12.1"),sQuery(id+"F0.wireOp",EDGE,"E9.12.2"),sQuery(id+"F0.wireOp",EDGE,"E9.12.3"),sQuery(id+"F0.wireOp",EDGE,"E9.12.4"),sQuery(id+"F0.wireOp",EDGE,"E9.13.0"),sQuery(id+"F0.wireOp",EDGE,"E9.13.1"),sQuery(id+"F0.wireOp",EDGE,"E9.13.2"),sQuery(id+"F0.wireOp",EDGE,"E9.13.3"),sQuery(id+"F0.wireOp",EDGE,"E9.13.4"),sQuery(id+"F0.wireOp",EDGE,"E9.14.0"),sQuery(id+"F0.wireOp",EDGE,"E9.14.1"),sQuery(id+"F0.wireOp",EDGE,"E9.14.2"),sQuery(id+"F0.wireOp",EDGE,"E9.14.3"),sQuery(id+"F0.wireOp",EDGE,"E9.14.4"),sQuery(id+"F0.wireOp",EDGE,"E9.15.0"),sQuery(id+"F0.wireOp",EDGE,"E9.15.1"),sQuery(id+"F0.wireOp",EDGE,"E9.15.2"),sQuery(id+"F0.wireOp",EDGE,"E9.15.3"),sQuery(id+"F0.wireOp",EDGE,"E9.15.4"),sQuery(id+"F0.wireOp",EDGE,"E9.16.0"),sQuery(id+"F0.wireOp",EDGE,"E9.16.1"),sQuery(id+"F0.wireOp",EDGE,"E9.16.2"),sQuery(id+"F0.wireOp",EDGE,"E9.16.3"),sQuery(id+"F0.wireOp",EDGE,"E9.16.4"),sQuery(id+"F0.wireOp",EDGE,"E9.17.0"),sQuery(id+"F0.wireOp",EDGE,"E9.17.1"),sQuery(id+"F0.wireOp",EDGE,"E9.17.2"),sQuery(id+"F0.wireOp",EDGE,"E9.17.3"),sQuery(id+"F0.wireOp",EDGE,"E9.17.4"),sQuery(id+"F0.wireOp",EDGE,"E9.18.0"),sQuery(id+"F0.wireOp",EDGE,"E9.18.1"),sQuery(id+"F0.wireOp",EDGE,"E9.18.2"),sQuery(id+"F0.wireOp",EDGE,"E9.18.3"),sQuery(id+"F0.wireOp",EDGE,"E9.18.4"),sQuery(id+"F0.wireOp",EDGE,"E9.19.0"),sQuery(id+"F0.wireOp",EDGE,"E9.19.1"),sQuery(id+"F0.wireOp",EDGE,"E9.19.2"),sQuery(id+"F0.wireOp",EDGE,"E9.19.3"),sQuery(id+"F0.wireOp",EDGE,"E9.19.4"),sQuery(id+"F0.wireOp",EDGE,"E9.20.0"),sQuery(id+"F0.wireOp",EDGE,"E9.20.1"),sQuery(id+"F0.wireOp",EDGE,"E9.20.2"),sQuery(id+"F0.wireOp",EDGE,"E9.20.3"),sQuery(id+"F0.wireOp",EDGE,"E9.20.4"),sQuery(id+"F0.wireOp",EDGE,"E9.21.0"),sQuery(id+"F0.wireOp",EDGE,"E9.21.1"),sQuery(id+"F0.wireOp",EDGE,"E9.21.2"),sQuery(id+"F0.wireOp",EDGE,"E9.21.3"),sQuery(id+"F0.wireOp",EDGE,"E9.21.4"),sQuery(id+"F0.wireOp",EDGE,"E9.22.0"),sQuery(id+"F0.wireOp",EDGE,"E9.22.1"),sQuery(id+"F0.wireOp",EDGE,"E9.22.2"),sQuery(id+"F0.wireOp",EDGE,"E9.22.3"),sQuery(id+"F0.wireOp",EDGE,"E9.22.4"),sQuery(id+"F0.wireOp",EDGE,"E9.23.0"),sQuery(id+"F0.wireOp",EDGE,"E9.23.1"),sQuery(id+"F0.wireOp",EDGE,"E9.23.2"),sQuery(id+"F0.wireOp",EDGE,"E9.23.3"),sQuery(id+"F0.wireOp",EDGE,"E9.23.4"),sQuery(id+"F0.wireOp",EDGE,"E9.24.0"),sQuery(id+"F0.wireOp",EDGE,"E9.24.1"),sQuery(id+"F0.wireOp",EDGE,"E9.24.2"),sQuery(id+"F0.wireOp",EDGE,"E9.24.3"),sQuery(id+"F0.wireOp",EDGE,"E9.24.4"),sQuery(id+"F0.wireOp",EDGE,"E9.25.0"),sQuery(id+"F0.wireOp",EDGE,"E9.25.1"),sQuery(id+"F0.wireOp",EDGE,"E9.25.2"),sQuery(id+"F0.wireOp",EDGE,"E9.25.3"),sQuery(id+"F0.wireOp",EDGE,"E9.25.4"),sQuery(id+"F0.wireOp",EDGE,"E9.26.0"),sQuery(id+"F0.wireOp",EDGE,"E9.26.1"),sQuery(id+"F0.wireOp",EDGE,"E9.26.2"),sQuery(id+"F0.wireOp",EDGE,"E9.26.3"),sQuery(id+"F0.wireOp",EDGE,"E9.26.4"),sQuery(id+"F0.wireOp",EDGE,"E9.27.0"),sQuery(id+"F0.wireOp",EDGE,"E9.27.1"),sQuery(id+"F0.wireOp",EDGE,"E9.27.2"),sQuery(id+"F0.wireOp",EDGE,"E9.27.3"),sQuery(id+"F0.wireOp",EDGE,"E9.27.4"),sQuery(id+"F0.wireOp",EDGE,"E9.28.0"),sQuery(id+"F0.wireOp",EDGE,"E9.28.1"),sQuery(id+"F0.wireOp",EDGE,"E9.28.2"),sQuery(id+"F0.wireOp",EDGE,"E9.28.3"),sQuery(id+"F0.wireOp",EDGE,"E9.28.4"),sQuery(id+"F0.wireOp",EDGE,"E9.29.0"),sQuery(id+"F0.wireOp",EDGE,"E9.29.1"),sQuery(id+"F0.wireOp",EDGE,"E9.29.2"),sQuery(id+"F0.wireOp",EDGE,"E9.29.3"),sQuery(id+"F0.wireOp",EDGE,"E9.29.4"),sQuery(id+"F0.wireOp",EDGE,"E9.30.0"),sQuery(id+"F0.wireOp",EDGE,"E9.30.1"),sQuery(id+"F0.wireOp",EDGE,"E9.30.2"),sQuery(id+"F0.wireOp",EDGE,"E9.30.3"),sQuery(id+"F0.wireOp",EDGE,"E9.30.4"),sQuery(id+"F0.wireOp",EDGE,"E9.31.0"),sQuery(id+"F0.wireOp",EDGE,"E9.31.1"),sQuery(id+"F0.wireOp",EDGE,"E9.31.2"),sQuery(id+"F0.wireOp",EDGE,"E9.31.3"),sQuery(id+"F0.wireOp",EDGE,"E9.31.4"),sQuery(id+"F0.wireOp",EDGE,"E9.32.0"),sQuery(id+"F0.wireOp",EDGE,"E9.32.1"),sQuery(id+"F0.wireOp",EDGE,"E9.32.2"),sQuery(id+"F0.wireOp",EDGE,"E9.32.3"),sQuery(id+"F0.wireOp",EDGE,"E9.32.4"),sQuery(id+"F0.wireOp",EDGE,"E9.33.0"),sQuery(id+"F0.wireOp",EDGE,"E9.33.1"),sQuery(id+"F0.wireOp",EDGE,"E9.33.2"),sQuery(id+"F0.wireOp",EDGE,"E9.33.3"),sQuery(id+"F0.wireOp",EDGE,"E9.33.4"),sQuery(id+"F0.wireOp",EDGE,"E9.34.0"),sQuery(id+"F0.wireOp",EDGE,"E9.34.1"),sQuery(id+"F0.wireOp",EDGE,"E9.34.2"),sQuery(id+"F0.wireOp",EDGE,"E9.34.3"),sQuery(id+"F0.wireOp",EDGE,"E9.34.4"),sQuery(id+"F0.wireOp",EDGE,"E9.35.0"),sQuery(id+"F0.wireOp",EDGE,"E9.35.1"),sQuery(id+"F0.wireOp",EDGE,"E9.35.2"),sQuery(id+"F0.wireOp",EDGE,"E9.35.3"),sQuery(id+"F0.wireOp",EDGE,"E9.35.4"),sQuery(id+"F0.wireOp",EDGE,"E11.trimOffspring"),sQuery(id+"F0.wireOp",EDGE,"E13.trimOffspring"),sQuery(id+"F0.wireOp",EDGE,"E15.trimOffspring"),sQuery(id+"F0.wireOp",EDGE,"E17.trimOffspring"),sQuery(id+"F0.wireOp",EDGE,"E18.trimOffspring"),sQuery(id+"F0.wireOp",EDGE,"E20.trimOffspring"),sQuery(id+"F0.wireOp",EDGE,"E22.trimOffspring"),sQuery(id+"F0.wireOp",EDGE,"E23.trimOffspring"),sQuery(id+"F0.wireOp",EDGE,"E25.trimOffspring"),sQuery(id+"F0.wireOp",EDGE,"E27.trimOffspring"),sQuery(id+"F0.wireOp",EDGE,"E28.trimOffspring"),sQuery(id+"F0.wireOp",EDGE,"E30.trimOffspring"),sQuery(id+"F0.wireOp",EDGE,"E31.trimOffspring"),sQuery(id+"F0.wireOp",EDGE,"E33.trimOffspring"),sQuery(id+"F0.wireOp",EDGE,"E35.trimOffspring"),sQuery(id+"F0.wireOp",EDGE,"E37.trimOffspring"),sQuery(id+"F0.wireOp",EDGE,"E39.trimOffspring"),sQuery(id+"F0.wireOp",EDGE,"E41.trimOffspring"),sQuery(id+"F0.wireOp",EDGE,"E43.trimOffspring"),sQuery(id+"F0.wireOp",EDGE,"E45.trimOffspring"),sQuery(id+"F0.wireOp",EDGE,"E47.trimOffspring"),sQuery(id+"F0.wireOp",EDGE,"E48.trimOffspring"),sQuery(id+"F0.wireOp",EDGE,"E50.trimOffspring"),sQuery(id+"F0.wireOp",EDGE,"E52.trimOffspring"),sQuery(id+"F0.wireOp",EDGE,"E54.trimOffspring"),sQuery(id+"F0.wireOp",EDGE,"E56.trimOffspring"),sQuery(id+"F0.wireOp",EDGE,"E58.trimOffspring"),sQuery(id+"F0.wireOp",EDGE,"E60.trimOffspring"),sQuery(id+"F0.wireOp",EDGE,"E62.trimOffspring"),sQuery(id+"F0.wireOp",EDGE,"E64.trimOffspring"),sQuery(id+"F0.wireOp",EDGE,"E65.trimOffspring"),sQuery(id+"F0.wireOp",EDGE,"E67.trimOffspring"),sQuery(id+"F0.wireOp",EDGE,"E69.trimOffspring"),sQuery(id+"F0.wireOp",EDGE,"E71.trimOffspring")])],"isStart":false});
            var sketch = newSketch(context, id + "F2", { "sketchPlane" : qUnion([Q0])});
            skCircle(sketch, "E73", {"center": v(0, 0) * mm, "radius": 11.43 * mm});
            skSolve(sketch);
        }
        {
            var Q0;
            Q0=makeQuery(id+"F2.imprint","IMPRINT",FACE,{"disambiguationData":[TD([[makeQuery(id+"F2.imprint","IMPRINT",EDGE,{"derivedFrom":sQuery(id+"F2.wireOp",EDGE,"E73")}),1.0]])]});
            extrude(context, id + "F3", {"entities" : qUnion([Q0]), "operationType" : NewBodyOperationType.ADD, "depth" : 7.37 * mm});
        }
        {
            var Q0;
            Q0=makeQuery(id+"F3.opExtrude","CAP_FACE",FACE,{"disambiguationData":[OSD([sQuery(id+"F2.wireOp",EDGE,"E73")])],"isStart":false});
            var sketch = newSketch(context, id + "F4", { "sketchPlane" : qUnion([Q0])});
            skCircle(sketch, "E74.cCircle", {"center": v(0, 0) * mm, "radius": 5.59 * mm, "construction": true});
            skLineSegment(sketch, "E74.0", {"start": v(6.45, -0.06) * mm, "end": v(3.18, -5.62) * mm});
            skLineSegment(sketch, "E74.1", {"start": v(3.18, -5.62) * mm, "end": v(-3.28, -5.56) * mm});
            skLineSegment(sketch, "E74.2", {"start": v(-3.28, -5.56) * mm, "end": v(-6.45, 0.06) * mm});
            skLineSegment(sketch, "E74.3", {"start": v(-6.45, 0.06) * mm, "end": v(-3.18, 5.62) * mm});
            skLineSegment(sketch, "E74.4", {"start": v(-3.18, 5.62) * mm, "end": v(3.28, 5.56) * mm});
            skLineSegment(sketch, "E74.5", {"start": v(3.28, 5.56) * mm, "end": v(6.45, -0.06) * mm});
            skPoint(sketch, "E74.0.midPoint", {"position": v(4.81, -2.84) * mm});
            skSolve(sketch);
        }
        {
            var Q0;
            Q0 = qSketchRegion(id + "F4", true);
            extrude(context, id + "F5", {"entities" : qUnion([Q0]), "operationType" : NewBodyOperationType.REMOVE, "oppositeDirection" : true, "depth" : 25.4 * mm});
        }
    });
